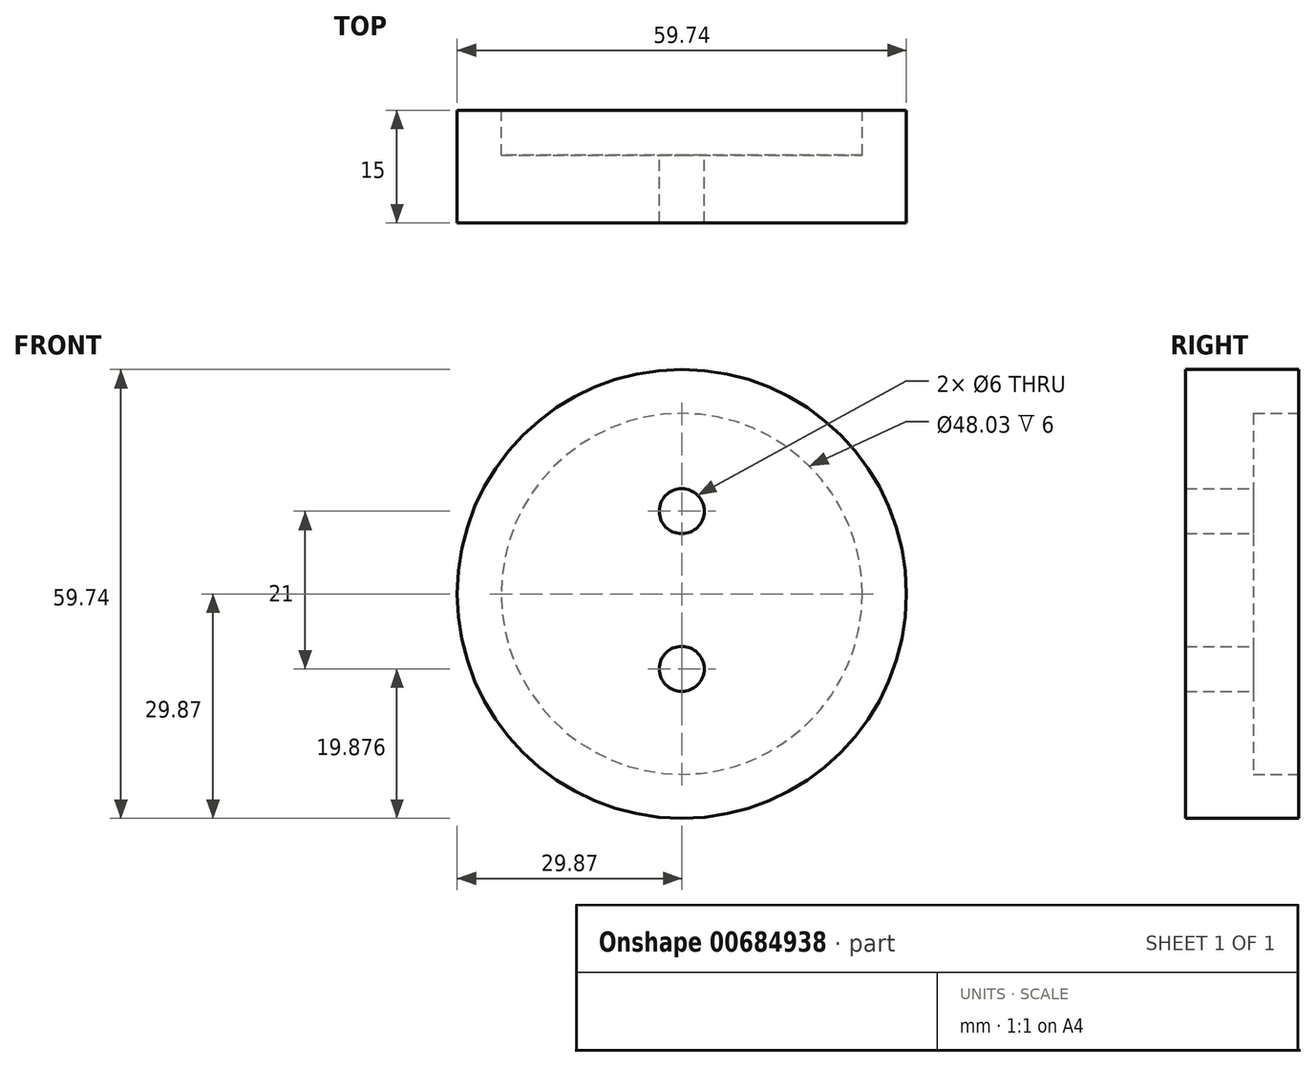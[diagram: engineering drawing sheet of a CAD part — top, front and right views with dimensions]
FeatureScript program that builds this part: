
annotation { "Feature Type Name" : "Feature", "Feature Type Description" : "" }
export const myFeature = defineFeature(function(context is Context, id is Id, definition is map)
    precondition{}
    {
        {
            var Q0;
            Q0=qCreatedBy(makeId("Front.planeOp"),FACE);
            var sketch = newSketch(context, id + "F0", { "sketchPlane" : qUnion([Q0])});
            skCircle(sketch, "E0", {"center": v(0, 0) * mm, "radius": 29.87 * mm});
            skSolve(sketch);
        }
        {
            var Q0;
            Q0 = qSketchRegion(id + "F0", true);
            extrude(context, id + "F1", {"entities" : qUnion([Q0]), "depth" : 15 * mm, "offsetDistance" : 25 * mm});
        }
        {
            var Q0;
            Q0=makeQuery(id+"F1.opExtrude","CAP_FACE",FACE,{"disambiguationData":[OSD([sQuery(id+"F0.wireOp",EDGE,"E0")])],"isStart":true});
            var sketch = newSketch(context, id + "F2", { "sketchPlane" : qUnion([Q0])});
            skCircle(sketch, "E1", {"center": v(0, 0) * mm, "radius": 24.02 * mm});
            skSolve(sketch);
        }
        {
            var Q0;
            Q0 = qSketchRegion(id + "F2", true);
            extrude(context, id + "F3", {"entities" : qUnion([Q0]), "operationType" : NewBodyOperationType.REMOVE, "oppositeDirection" : true, "depth" : 6 * mm, "offsetDistance" : 25 * mm});
        }
        {
            var Q0;
            Q0=makeQuery(id+"F3.boolean.opBoolean","COPY",FACE,{"derivedFrom":makeQuery(id+"F3.opExtrude","CAP_FACE",FACE,{"disambiguationData":[OSD([sQuery(id+"F2.wireOp",EDGE,"E1")])],"isStart":false})});
            var sketch = newSketch(context, id + "F4", { "sketchPlane" : qUnion([Q0])});
            skCircle(sketch, "E2", {"center": v(0, 11) * mm, "radius": 3 * mm});
            skCircle(sketch, "E3", {"center": v(0, -10) * mm, "radius": 3 * mm});
            skSolve(sketch);
        }
        {
            var Q0;
            Q0=makeQuery(id+"F4.imprint","IMPRINT",FACE,{"disambiguationData":[TD([[makeQuery(id+"F4.imprint","IMPRINT",EDGE,{"derivedFrom":sQuery(id+"F4.wireOp",EDGE,"E2")}),1.0]])]});
            var Q1;
            Q1=makeQuery(id+"F4.imprint","IMPRINT",FACE,{"disambiguationData":[TD([[makeQuery(id+"F4.imprint","IMPRINT",EDGE,{"derivedFrom":sQuery(id+"F4.wireOp",EDGE,"E3")}),1.0]])]});
            extrude(context, id + "F5", {"entities" : qUnion([Q0, Q1]), "operationType" : NewBodyOperationType.REMOVE, "oppositeDirection" : true, "depth" : 25 * mm, "offsetDistance" : 25 * mm});
        }
    });
